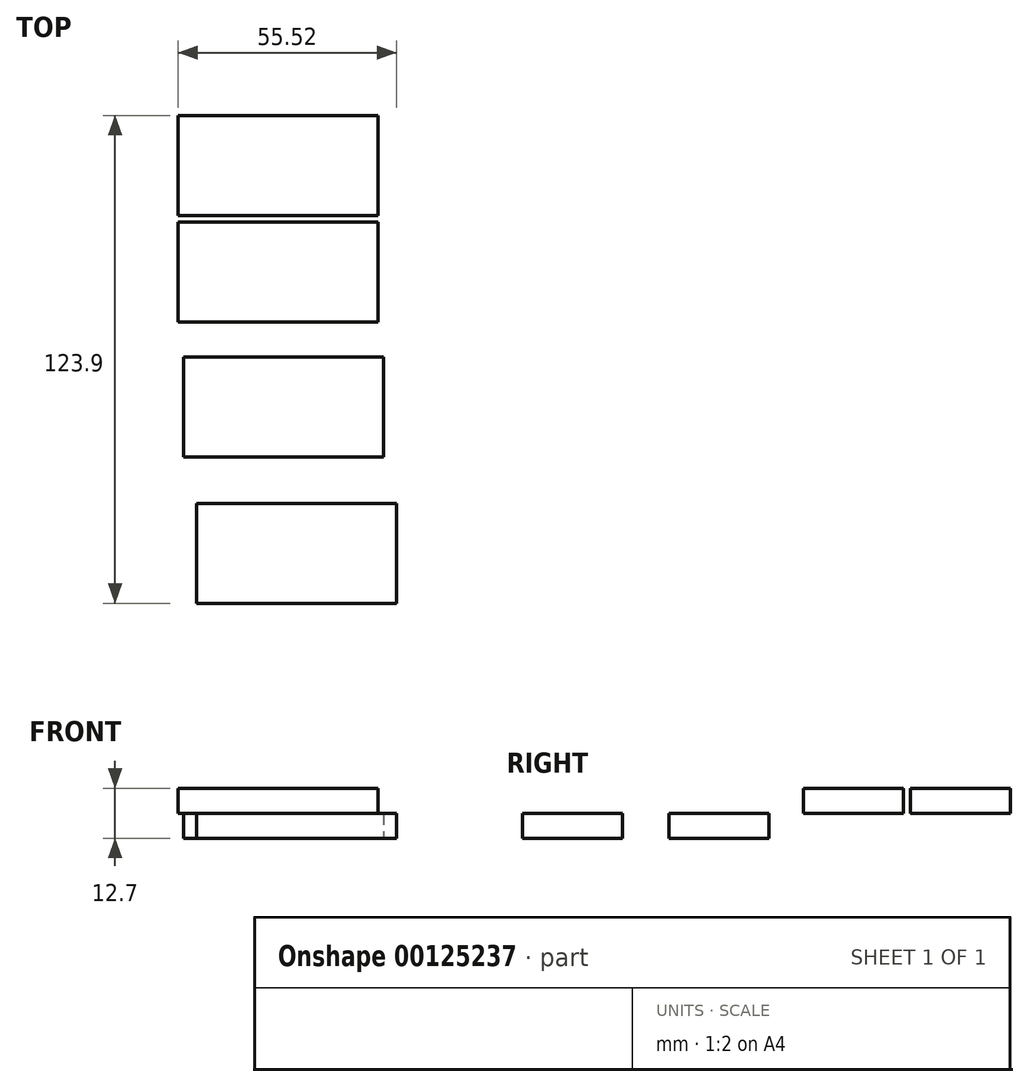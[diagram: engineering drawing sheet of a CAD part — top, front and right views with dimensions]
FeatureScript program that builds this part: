
annotation { "Feature Type Name" : "Feature", "Feature Type Description" : "" }
export const myFeature = defineFeature(function(context is Context, id is Id, definition is map)
    precondition{}
    {
        {
            var Q0;
            Q0=qCreatedBy(makeId("Top.planeOp"),FACE);
            var sketch = newSketch(context, id + "F0", { "sketchPlane" : qUnion([Q0])});
            skLineSegment(sketch, "E0.bottom", {"start": v(25.4, -12.7) * mm, "end": v(-25.4, -12.7) * mm});
            skLineSegment(sketch, "E0.top", {"start": v(25.4, 12.7) * mm, "end": v(-25.4, 12.7) * mm});
            skLineSegment(sketch, "E0.left", {"start": v(25.4, -12.7) * mm, "end": v(25.4, 12.7) * mm});
            skLineSegment(sketch, "E0.right", {"start": v(-25.4, -12.7) * mm, "end": v(-25.4, 12.7) * mm});
            skPoint(sketch, "E0.middle", {"position": v(0, 0) * mm});
            skSolve(sketch);
        }
        {
            var Q0;
            Q0=makeQuery(id+"F0.imprint","IMPRINT",FACE,{"disambiguationData":[TD([[makeQuery(id+"F0.imprint","IMPRINT",EDGE,{"derivedFrom":sQuery(id+"F0.wireOp",EDGE,"E0.bottom")}),-1.0]])]});
            extrude(context, id + "F1", {"entities" : qUnion([Q0]), "depth" : 6.35 * mm});
        }
        {
            var Q0;
            Q0=makeQuery(id+"F1.opExtrude","CAP_FACE",FACE,{"disambiguationData":[OSD([sQuery(id+"F0.wireOp",EDGE,"E0.bottom"),sQuery(id+"F0.wireOp",EDGE,"E0.top"),sQuery(id+"F0.wireOp",EDGE,"E0.left"),sQuery(id+"F0.wireOp",EDGE,"E0.right")])],"isStart":false});
            var sketch = newSketch(context, id + "F2", { "sketchPlane" : qUnion([Q0])});
            skLineSegment(sketch, "E1.bottom", {"start": v(-26.82, 46.87) * mm, "end": v(23.98, 46.87) * mm});
            skLineSegment(sketch, "E1.top", {"start": v(-26.82, 21.47) * mm, "end": v(23.98, 21.47) * mm});
            skLineSegment(sketch, "E1.left", {"start": v(-26.82, 46.87) * mm, "end": v(-26.82, 21.47) * mm});
            skLineSegment(sketch, "E1.right", {"start": v(23.98, 46.87) * mm, "end": v(23.98, 21.47) * mm});
            skLineSegment(sketch, "E2.bottom", {"start": v(-26.82, -24.73) * mm, "end": v(23.98, -24.73) * mm});
            skLineSegment(sketch, "E2.top", {"start": v(-26.82, -50.13) * mm, "end": v(23.98, -50.13) * mm});
            skLineSegment(sketch, "E2.left", {"start": v(-26.82, -24.73) * mm, "end": v(-26.82, -50.13) * mm});
            skLineSegment(sketch, "E2.right", {"start": v(23.98, -24.73) * mm, "end": v(23.98, -50.13) * mm});
            skLineSegment(sketch, "E3.bottom", {"start": v(-26.82, 73.97) * mm, "end": v(23.98, 73.97) * mm});
            skLineSegment(sketch, "E3.top", {"start": v(-26.82, 48.57) * mm, "end": v(23.98, 48.57) * mm});
            skLineSegment(sketch, "E3.left", {"start": v(-26.82, 73.97) * mm, "end": v(-26.82, 48.57) * mm});
            skLineSegment(sketch, "E3.right", {"start": v(23.98, 73.97) * mm, "end": v(23.98, 48.57) * mm});
            skSolve(sketch);
        }
        {
            var Q0;
            Q0=makeQuery(id+"F2.imprint","IMPRINT",FACE,{"disambiguationData":[TD([[makeQuery(id+"F2.imprint","IMPRINT",EDGE,{"derivedFrom":sQuery(id+"F2.wireOp",EDGE,"E3.bottom")}),-1.0]])]});
            var Q1;
            Q1=makeQuery(id+"F2.imprint","IMPRINT",FACE,{"disambiguationData":[TD([[makeQuery(id+"F2.imprint","IMPRINT",EDGE,{"derivedFrom":sQuery(id+"F2.wireOp",EDGE,"E1.bottom")}),-1.0]])]});
            extrude(context, id + "F3", {"entities" : qUnion([Q0, Q1]), "depth" : 6.35 * mm});
        }
        {
            var Q0;
            Q0=qCreatedBy(makeId("Top.planeOp"),FACE);
            var sketch = newSketch(context, id + "F4", { "sketchPlane" : qUnion([Q0])});
            skLineSegment(sketch, "E4.bottom", {"start": v(-22.1, -24.53) * mm, "end": v(28.7, -24.53) * mm});
            skLineSegment(sketch, "E4.top", {"start": v(-22.1, -49.93) * mm, "end": v(28.7, -49.93) * mm});
            skLineSegment(sketch, "E4.left", {"start": v(-22.1, -24.53) * mm, "end": v(-22.1, -49.93) * mm});
            skLineSegment(sketch, "E4.right", {"start": v(28.7, -24.53) * mm, "end": v(28.7, -49.93) * mm});
            skSolve(sketch);
        }
        {
            var Q0;
            Q0=makeQuery(id+"F4.imprint","IMPRINT",FACE,{"disambiguationData":[TD([[makeQuery(id+"F4.imprint","IMPRINT",EDGE,{"derivedFrom":sQuery(id+"F4.wireOp",EDGE,"E4.bottom")}),-1.0]])]});
            extrude(context, id + "F5", {"entities" : qUnion([Q0]), "depth" : 6.35 * mm});
        }
        {
            var Q0;
            Q0=makeQuery(id+"F1.opExtrude","SWEPT_BODY",BODY,{"disambiguationData":[OSD([sQuery(id+"F0.wireOp",EDGE,"E0.bottom"),sQuery(id+"F0.wireOp",EDGE,"E0.top"),sQuery(id+"F0.wireOp",EDGE,"E0.left"),sQuery(id+"F0.wireOp",EDGE,"E0.right")])]});
            transform(context, id + "F6", {"entities" : qUnion([Q0]), "transformType" : TransformType.TRANSLATION_3D, "dx" : 0 * mm, "dy" : 0 * mm, "dz" : 0 * mm, "makeCopy" : true});
        }
        {
            var Q0;
            Q0=makeQuery(id+"F1.opExtrude","SWEPT_BODY",BODY,{"disambiguationData":[OSD([sQuery(id+"F0.wireOp",EDGE,"E0.bottom"),sQuery(id+"F0.wireOp",EDGE,"E0.top"),sQuery(id+"F0.wireOp",EDGE,"E0.left"),sQuery(id+"F0.wireOp",EDGE,"E0.right")])]});
            transform(context, id + "F7", {"entities" : qUnion([Q0]), "transformType" : TransformType.TRANSLATION_3D, "dx" : 0 * mm, "dy" : 0 * mm, "dz" : 0 * mm, "makeCopy" : true});
        }
    });
